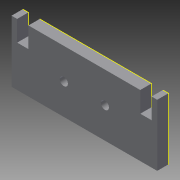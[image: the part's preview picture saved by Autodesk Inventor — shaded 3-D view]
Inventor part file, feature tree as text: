
AUTODESK INVENTOR PART (.ipt)
format: ipt  version: 2014 SP1 (Build 180222100, 222)  size: 128,000 bytes
history: native  units: mm
features: sketch x4, extrude x3
ambient origin geometry x8: Origin, YZ Plane, XZ Plane, XY Plane, X Axis, Y Axis, Z Axis, Center Point
bodies: Solid1 (feature_tree)
feature tree (7):
  extrude  "Extrusion1"  Depth=5.5mm TaperAngle=0.0deg
  extrude  "Extrusion2"  Depth=5.5mm
  sketch  "Sketch4"  dims[d7=10.0mm d8=30.0mm]
  extrude  "Extrusion3"  Depth=30.0mm
  sketch  "Sketch1"  dims[d0=71.0mm d1=5.5mm d2=0.0mm]
  sketch  "Sketch3"  dims[d5=30.0mm d6=5.5mm]
  sketch  "Sketch5"  dims[d9=3.0mm d10=0.0mm d11=4.0mm d12=20.0mm d13=10.0mm d14=0.0mm]
